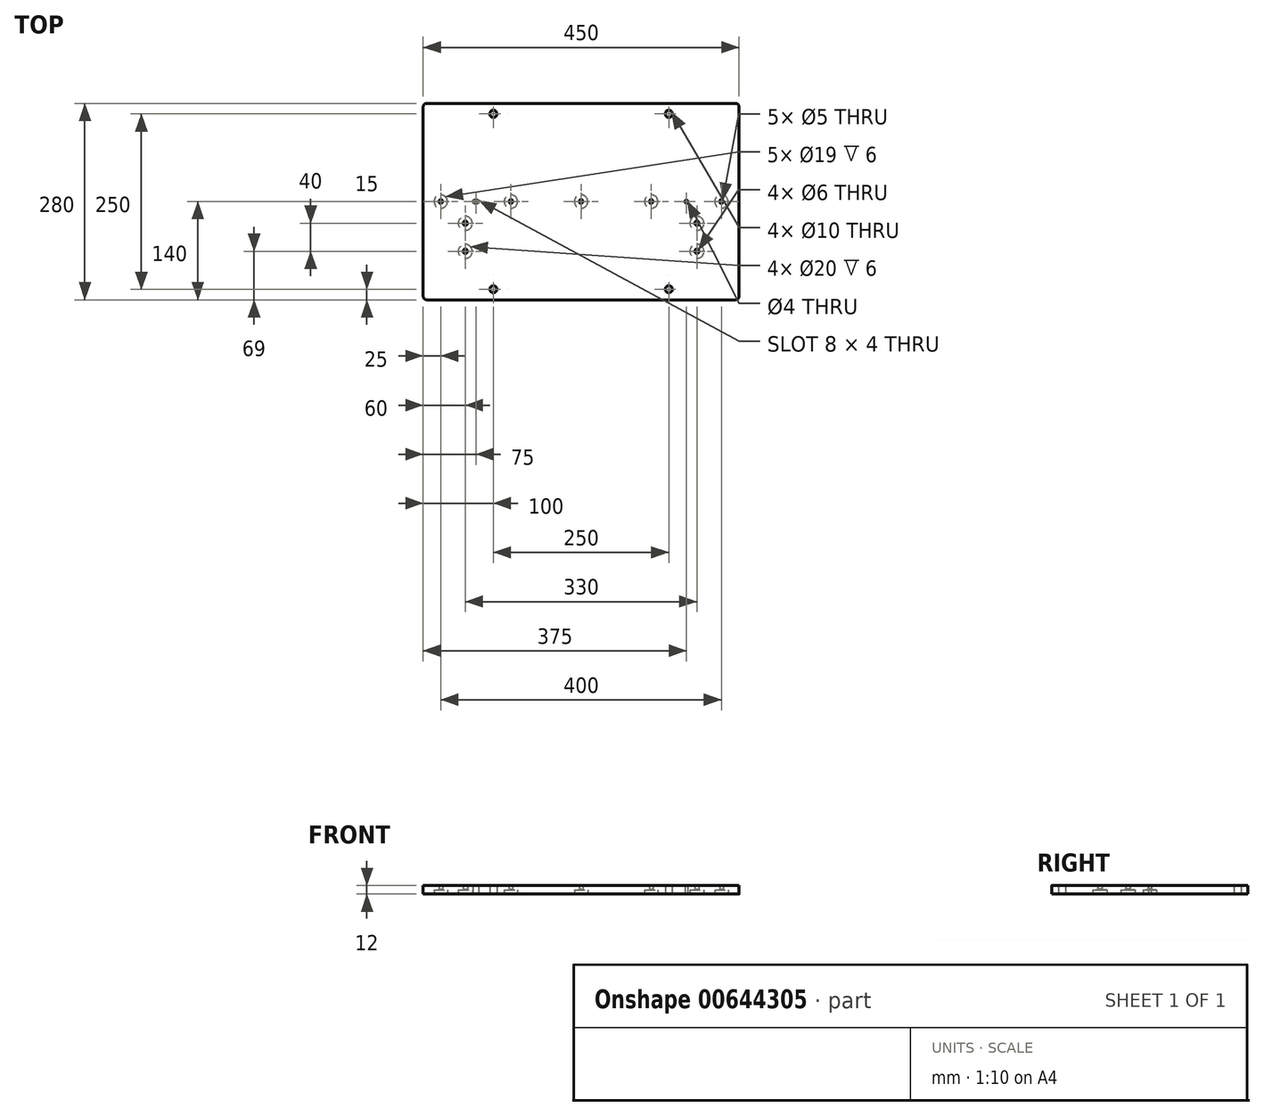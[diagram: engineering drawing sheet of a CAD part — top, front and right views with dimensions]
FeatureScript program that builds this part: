
annotation { "Feature Type Name" : "Feature", "Feature Type Description" : "" }
export const myFeature = defineFeature(function(context is Context, id is Id, definition is map)
    precondition{}
    {
        {
            var Q0;
            Q0=qCreatedBy(makeId("Top.planeOp"),FACE);
            var sketch = newSketch(context, id + "F0", { "sketchPlane" : qUnion([Q0])});
            skLineSegment(sketch, "E0.bottom", {"start": v(-225, 140) * mm, "end": v(225, 140) * mm});
            skLineSegment(sketch, "E0.top", {"start": v(-225, -140) * mm, "end": v(225, -140) * mm});
            skLineSegment(sketch, "E0.left", {"start": v(-225, 140) * mm, "end": v(-225, -140) * mm});
            skLineSegment(sketch, "E0.right", {"start": v(225, 140) * mm, "end": v(225, -140) * mm});
            skCircle(sketch, "E1", {"center": v(-125, 125) * mm, "radius": 5 * mm});
            skCircle(sketch, "E2", {"center": v(125, 125) * mm, "radius": 5 * mm});
            skCircle(sketch, "E3", {"center": v(-125, -125) * mm, "radius": 5 * mm});
            skCircle(sketch, "E4", {"center": v(125, -125) * mm, "radius": 5 * mm});
            skLineSegment(sketch, "E5", {"start": v(-228.53, 125) * mm, "end": v(501.46, 125) * mm, "construction": true});
            skLineSegment(sketch, "E6", {"start": v(-226.26, -125) * mm, "end": v(437.23, -125) * mm});
            skLineSegment(sketch, "E7", {"start": v(-125, 236.48) * mm, "end": v(-125, -151.94) * mm, "construction": true});
            skLineSegment(sketch, "E8", {"start": v(125, 244.8) * mm, "end": v(125, -172.35) * mm, "construction": true});
            skLineSegment(sketch, "E9", {"start": v(-454.18, 0) * mm, "end": v(381.6, 0) * mm, "construction": true});
            skCircle(sketch, "E10", {"center": v(100, 0) * mm, "radius": 2.5 * mm});
            skCircle(sketch, "E11", {"center": v(200, 0) * mm, "radius": 2.5 * mm});
            skLineSegment(sketch, "E12", {"start": v(0, 197.18) * mm, "end": v(0, -245.65) * mm, "construction": true});
            skCircle(sketch, "E13", {"center": v(0, 0) * mm, "radius": 2.5 * mm});
            skCircle(sketch, "E14.MirrorC", {"center": v(-100, 0) * mm, "radius": 2.5 * mm});
            skCircle(sketch, "E15.MirrorC", {"center": v(-200, 0) * mm, "radius": 2.5 * mm});
            skLineSegment(sketch, "E16", {"start": v(-331.04, -31) * mm, "end": v(392.1, -31) * mm, "construction": true});
            skLineSegment(sketch, "E17", {"start": v(-331.53, -71) * mm, "end": v(392.02, -71) * mm, "construction": true});
            skLineSegment(sketch, "E18", {"start": v(-165, 230.23) * mm, "end": v(-165, -171.96) * mm});
            skLineSegment(sketch, "E19", {"start": v(165, 226.24) * mm, "end": v(165, -215.47) * mm});
            skCircle(sketch, "E20", {"center": v(165, -31) * mm, "radius": 3 * mm});
            skCircle(sketch, "E21", {"center": v(165, -71) * mm, "radius": 3 * mm});
            skCircle(sketch, "E22", {"center": v(-165, -31) * mm, "radius": 3 * mm});
            skCircle(sketch, "E23", {"center": v(-165, -71) * mm, "radius": 3 * mm});
            skArc(sketch, "E24", {"start": v(-148, -2) * mm, "mid": v(-146, 0) * mm, "end": v(-148, 2) * mm});
            skCircle(sketch, "E25", {"center": v(150, 0) * mm, "radius": 2 * mm});
            skLineSegment(sketch, "E26", {"start": v(-148, 2) * mm, "end": v(-152, 2) * mm});
            skArc(sketch, "E27", {"start": v(-152, 2) * mm, "mid": v(-154, 0) * mm, "end": v(-152, -2) * mm});
            skLineSegment(sketch, "E28", {"start": v(-152, -2) * mm, "end": v(-148, -2) * mm});
            skSolve(sketch);
        }
        {
            var Q0;
            Q0 = qSketchRegion(id + "F0", true);
            extrude(context, id + "F1", {"entities" : qUnion([Q0]), "depth" : 12 * mm, "offsetDistance" : 25 * mm});
        }
        {
            var Q0;
            Q0=makeQuery(id+"F1.opExtrude","CAP_FACE",FACE,{"disambiguationData":[OSD([sQuery(id+"F0.wireOp",EDGE,"E0.bottom"),sQuery(id+"F0.wireOp",EDGE,"E0.top"),sQuery(id+"F0.wireOp",EDGE,"E0.left"),sQuery(id+"F0.wireOp",EDGE,"E0.right"),sQuery(id+"F0.wireOp",EDGE,"E1"),sQuery(id+"F0.wireOp",EDGE,"E2"),sQuery(id+"F0.wireOp",EDGE,"E3"),sQuery(id+"F0.wireOp",EDGE,"E4"),sQuery(id+"F0.wireOp",EDGE,"E10"),sQuery(id+"F0.wireOp",EDGE,"E11"),sQuery(id+"F0.wireOp",EDGE,"E13"),sQuery(id+"F0.wireOp",EDGE,"E14.MirrorC"),sQuery(id+"F0.wireOp",EDGE,"E15.MirrorC"),sQuery(id+"F0.wireOp",EDGE,"E20"),sQuery(id+"F0.wireOp",EDGE,"E21"),sQuery(id+"F0.wireOp",EDGE,"E22"),sQuery(id+"F0.wireOp",EDGE,"E23")])],"isStart":true});
            var sketch = newSketch(context, id + "F2", { "sketchPlane" : qUnion([Q0])});
            skCircle(sketch, "E29.0", {"center": v(-165, 71) * mm, "radius": 10 * mm});
            skCircle(sketch, "E30.0", {"center": v(165, 71) * mm, "radius": 10 * mm});
            skCircle(sketch, "E31.0", {"center": v(165, 31) * mm, "radius": 10 * mm});
            skCircle(sketch, "E32.0", {"center": v(-165, 31) * mm, "radius": 10 * mm});
            skCircle(sketch, "E33.0", {"center": v(-100, 0) * mm, "radius": 9.5 * mm});
            skCircle(sketch, "E34.0", {"center": v(-200, 0) * mm, "radius": 9.5 * mm});
            skCircle(sketch, "E35.0", {"center": v(100, 0) * mm, "radius": 9.5 * mm});
            skCircle(sketch, "E36.0", {"center": v(0, 0) * mm, "radius": 9.5 * mm});
            skCircle(sketch, "E37.0", {"center": v(200, 0) * mm, "radius": 9.5 * mm});
            skSolve(sketch);
        }
        {
            var Q0;
            Q0 = qSketchRegion(id + "F2", true);
            extrude(context, id + "F3", {"entities" : qUnion([Q0]), "operationType" : NewBodyOperationType.REMOVE, "oppositeDirection" : true, "depth" : 6 * mm, "offsetDistance" : 25 * mm});
        }
        {
            var Q0;
            Q0=makeQuery(id+"F1.opExtrude","SWEPT_EDGE",EDGE,{"disambiguationData":[OSD([sQuery(id+"F0.wireOp",EDGE,"E0.top"),sQuery(id+"F0.wireOp",EDGE,"E0.left")])]});
            var Q1;
            Q1=makeQuery(id+"F1.opExtrude","SWEPT_EDGE",EDGE,{"disambiguationData":[OSD([sQuery(id+"F0.wireOp",EDGE,"E0.top"),sQuery(id+"F0.wireOp",EDGE,"E0.right")])]});
            var Q2;
            Q2=makeQuery(id+"F1.opExtrude","SWEPT_EDGE",EDGE,{"disambiguationData":[OSD([sQuery(id+"F0.wireOp",EDGE,"E0.bottom"),sQuery(id+"F0.wireOp",EDGE,"E0.right")])]});
            var Q3;
            Q3=makeQuery(id+"F1.opExtrude","SWEPT_EDGE",EDGE,{"disambiguationData":[OSD([sQuery(id+"F0.wireOp",EDGE,"E0.bottom"),sQuery(id+"F0.wireOp",EDGE,"E0.left")])]});
            fillet(context, id + "F4", {"entities" : qUnion([Q0, Q1, Q2, Q3]), "radius" : 5 * mm, "tangentPropagation" : true, "allowEdgeOverflow" : false});
        }
        {
            var Q0;
            Q0=makeQuery(id+"F3.boolean.opBoolean","INTERSECT",EDGE,{"derivedFrom":[makeQuery(id+"F1.opExtrude","SWEPT_FACE",FACE,{"disambiguationData":[OSD([sQuery(id+"F0.wireOp",EDGE,"E11")])]}),makeQuery(id+"F3.opExtrude","CAP_FACE",FACE,{"disambiguationData":[OSD([sQuery(id+"F2.wireOp",EDGE,"E37.0")])],"isStart":false})]});
            var Q1;
            Q1=makeQuery(id+"F3.boolean.opBoolean","INTERSECT",EDGE,{"derivedFrom":[makeQuery(id+"F1.opExtrude","SWEPT_FACE",FACE,{"disambiguationData":[OSD([sQuery(id+"F0.wireOp",EDGE,"E10")])]}),makeQuery(id+"F3.opExtrude","CAP_FACE",FACE,{"disambiguationData":[OSD([sQuery(id+"F2.wireOp",EDGE,"E35.0")])],"isStart":false})]});
            var Q2;
            Q2=makeQuery(id+"F3.boolean.opBoolean","INTERSECT",EDGE,{"derivedFrom":[makeQuery(id+"F1.opExtrude","SWEPT_FACE",FACE,{"disambiguationData":[OSD([sQuery(id+"F0.wireOp",EDGE,"E15.MirrorC")])]}),makeQuery(id+"F3.opExtrude","CAP_FACE",FACE,{"disambiguationData":[OSD([sQuery(id+"F2.wireOp",EDGE,"E34.0")])],"isStart":false})]});
            var Q3;
            Q3=makeQuery(id+"F3.boolean.opBoolean","INTERSECT",EDGE,{"derivedFrom":[makeQuery(id+"F1.opExtrude","SWEPT_FACE",FACE,{"disambiguationData":[OSD([sQuery(id+"F0.wireOp",EDGE,"E14.MirrorC")])]}),makeQuery(id+"F3.opExtrude","CAP_FACE",FACE,{"disambiguationData":[OSD([sQuery(id+"F2.wireOp",EDGE,"E33.0")])],"isStart":false})]});
            var Q4;
            Q4=makeQuery(id+"F3.boolean.opBoolean","INTERSECT",EDGE,{"derivedFrom":[makeQuery(id+"F1.opExtrude","SWEPT_FACE",FACE,{"disambiguationData":[OSD([sQuery(id+"F0.wireOp",EDGE,"E13")])]}),makeQuery(id+"F3.opExtrude","CAP_FACE",FACE,{"disambiguationData":[OSD([sQuery(id+"F2.wireOp",EDGE,"E36.0")])],"isStart":false})]});
            var Q5;
            Q5=makeQuery(id+"F3.boolean.opBoolean","INTERSECT",EDGE,{"derivedFrom":[makeQuery(id+"F1.opExtrude","SWEPT_FACE",FACE,{"disambiguationData":[OSD([sQuery(id+"F0.wireOp",EDGE,"E21")])]}),makeQuery(id+"F3.opExtrude","CAP_FACE",FACE,{"disambiguationData":[OSD([sQuery(id+"F2.wireOp",EDGE,"E30.0")])],"isStart":false})]});
            var Q6;
            Q6=makeQuery(id+"F3.boolean.opBoolean","INTERSECT",EDGE,{"derivedFrom":[makeQuery(id+"F1.opExtrude","SWEPT_FACE",FACE,{"disambiguationData":[OSD([sQuery(id+"F0.wireOp",EDGE,"E20")])]}),makeQuery(id+"F3.opExtrude","CAP_FACE",FACE,{"disambiguationData":[OSD([sQuery(id+"F2.wireOp",EDGE,"E31.0")])],"isStart":false})]});
            var Q7;
            Q7=makeQuery(id+"F1.opExtrude","CAP_EDGE",EDGE,{"disambiguationData":[OSD([sQuery(id+"F0.wireOp",EDGE,"E2")])],"isStart":true});
            var Q8;
            Q8=makeQuery(id+"F1.opExtrude","CAP_EDGE",EDGE,{"disambiguationData":[OSD([sQuery(id+"F0.wireOp",EDGE,"E1")])],"isStart":true});
            var Q9;
            Q9=makeQuery(id+"F3.boolean.opBoolean","INTERSECT",EDGE,{"derivedFrom":[makeQuery(id+"F1.opExtrude","SWEPT_FACE",FACE,{"disambiguationData":[OSD([sQuery(id+"F0.wireOp",EDGE,"E22")])]}),makeQuery(id+"F3.opExtrude","CAP_FACE",FACE,{"disambiguationData":[OSD([sQuery(id+"F2.wireOp",EDGE,"E32.0")])],"isStart":false})]});
            var Q10;
            Q10=makeQuery(id+"F3.boolean.opBoolean","INTERSECT",EDGE,{"derivedFrom":[makeQuery(id+"F1.opExtrude","SWEPT_FACE",FACE,{"disambiguationData":[OSD([sQuery(id+"F0.wireOp",EDGE,"E23")])]}),makeQuery(id+"F3.opExtrude","CAP_FACE",FACE,{"disambiguationData":[OSD([sQuery(id+"F2.wireOp",EDGE,"E29.0")])],"isStart":false})]});
            chamfer(context, id + "F5", {"entities" : qUnion([Q0, Q1, Q2, Q3, Q4, Q5, Q6, Q7, Q8, Q9, Q10]), "width" : 1 * mm, "tangentPropagation" : true});
        }
    });
